# Revit family: RN 90060 Optifitt-Serra-Wasserzähler-Bogen
name_source: partatom
category: Rohrformteile
units: mm (PartAtom-declared; Revit-internal decimal feet)

## family parameters
Arbeitsebenenbasiert = Nein
Beim Laden mit Abzugskörper schneiden = Nein
Bemaßung runder Anschluss = Durchmesser verwenden
Gemeinsam genutzt = Nein
Immer vertikal = Ja
Teiletyp = Bogen

## types (4) — shared parameters
1.010.00.2 Blattnummer der Richtlinie = 29
1.010.00.3 Ausgabedatum (Monat) der Richtlinie = 201308
1.010.00.4 Herstellername = R. Nussbaum AG
1.010.00.5 Revisionsdatum der Datei = 20190521
1.010.00.6 Webadresse des Herstellers = http://www.nussbaum.ch
1.100.00.4 Produktbezeichnung = Versorgung
1.110.00.2 Index = 3
1.110.00.4 Produktbezeichnung = Optifitt-Serra
1.960/3L.00.8 Link (URL) = https://www.nussbaum.ch
29.700.00.4 Produktname = Optifitt-Serra-Wasserzähler-Bogen, mit Innengewinde
29.700.00.5 Produktkennung = 2
29.700.00.6 Querschnittsform = 1
29.700.00.7 Nennweitensystem = DN
29.700.00.8 Nenndrucksystem = PN
29.710.02.4 Nenndruck = 16
29.710.02.5 max. zul. Überdruck [hPa] = 1600
29.710.02.7 max. zul. Dauer-Betriebsdruck [hPa] = 1600
29.710.02.9 max. zul. Dauer-Betriebstemperatur [°C] = 90
EnclosingSpace Visibility = Nein
Hersteller = R. Nussbaum AG
URL = https://www.nussbaum.ch

## per-type parameters (varying)
| type | 1.800.00.3 TGA-Nummer | 1.800.00.4 Kommentarfeld | 1.810.00.3 Hersteller-Bestellnummer | 1.810.00.4 DATANORM-Nummer | 1.810.00.5 StLB-Nummer | 1.810.00.6 GTIN-Nummer | 29.710.02.10 Formstück-Gewicht [kg] | 29.710.02.3 Benennung | Modell | R. Nussbaum AG 90060.05 de Visibility | R. Nussbaum AG 90060.06 de Visibility | R. Nussbaum AG 90060.07 de Visibility | R. Nussbaum AG 90060.08 de Visibility | Typenkommentare |
| DN=40 | 01900300000000000000000000000000000000000000000028???000000000000004 | 90060.08, Optifitt-Serra-Wasserzähler-Bogen, mit Innengewinde, DN=40, L=57, Rp=1½ | 90060.08 | 90060.08 | 216.516 | 7612945035516 | 1.779 | Optifitt-Serra-Wasserzähler-Bogen, mit Innengewinde, DN=40, L=57, Rp=1½ | 90060.08 | Nein | Nein | Nein | Ja | Optifitt-Serra-Wasserzähler-Bogen  DN=40 |
| DN=32 | 01900300000000000000000000000000000000000000000028???000000000000003 | 90060.07, Optifitt-Serra-Wasserzähler-Bogen, mit Innengewinde, DN=32, L=89, Rp=1¼ | 90060.07 | 90060.07 | 216.515 | 7612945035509 | 1.583 | Optifitt-Serra-Wasserzähler-Bogen, mit Innengewinde, DN=32, L=89, Rp=1¼ | 90060.07 | Nein | Nein | Ja | Nein | Optifitt-Serra-Wasserzähler-Bogen  DN=32 |
| DN=25 | 01900300000000000000000000000000000000000000000028???000000000000002 | 90060.06, Optifitt-Serra-Wasserzähler-Bogen, mit Innengewinde, DN=25, L=87, Rp=1 | 90060.06 | 90060.06 | 216.514 | 7612945035493 | 1.427 | Optifitt-Serra-Wasserzähler-Bogen, mit Innengewinde, DN=25, L=87, Rp=1 | 90060.06 | Nein | Ja | Nein | Nein | Optifitt-Serra-Wasserzähler-Bogen  DN=25 |
| DN=20 | 01900300000000000000000000000000000000000000000028???000000000000001 | 90060.05, Optifitt-Serra-Wasserzähler-Bogen, mit Innengewinde, DN=20, L=115, Rp=¾ | 90060.05 | 90060.05 | 216.513 | 7612945035486 | 1.373 | Optifitt-Serra-Wasserzähler-Bogen, mit Innengewinde, DN=20, L=115, Rp=¾ | 90060.05 | Ja | Nein | Nein | Nein | Optifitt-Serra-Wasserzähler-Bogen  DN=20 |

## geometry (parser evidence)
native form markers: Sweep x2
no freeform markers — native parametric forms only
